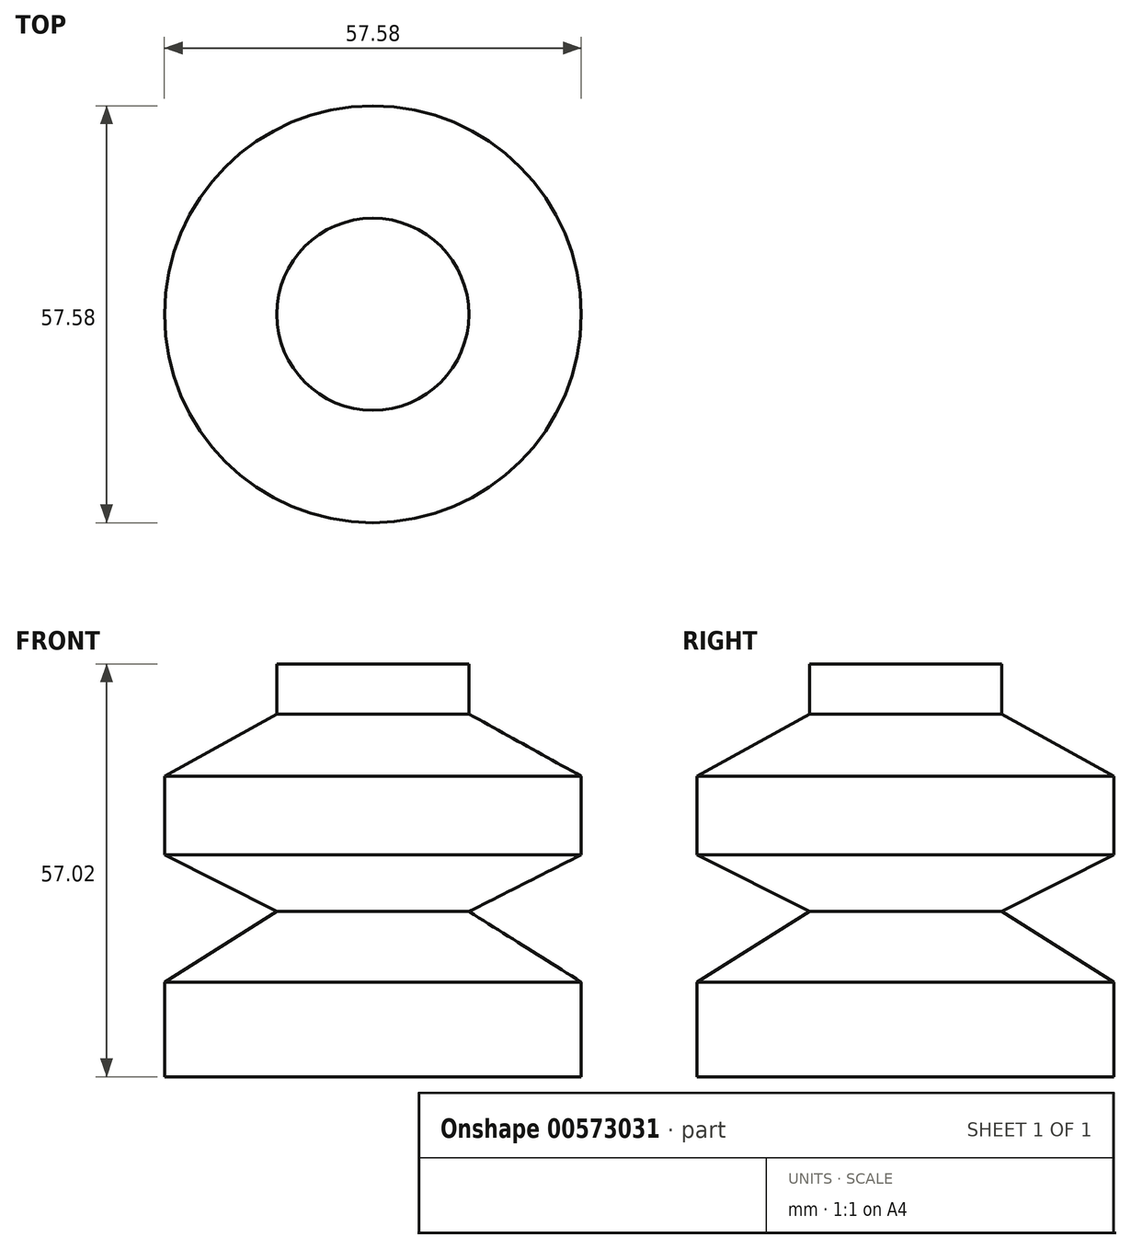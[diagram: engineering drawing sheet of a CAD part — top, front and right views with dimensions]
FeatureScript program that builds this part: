
annotation { "Feature Type Name" : "Feature", "Feature Type Description" : "" }
export const myFeature = defineFeature(function(context is Context, id is Id, definition is map)
    precondition{}
    {
        {
            var Q0;
            Q0=qCreatedBy(makeId("Front.planeOp"),FACE);
            var sketch = newSketch(context, id + "F0", { "sketchPlane" : qUnion([Q0])});
            skLineSegment(sketch, "E0", {"start": v(0, 0) * mm, "end": v(-28.79, 0) * mm});
            skLineSegment(sketch, "E1", {"start": v(-28.79, 0) * mm, "end": v(-28.79, 13.09) * mm});
            skLineSegment(sketch, "E2", {"start": v(-28.79, 13.09) * mm, "end": v(-13.27, 22.8) * mm});
            skLineSegment(sketch, "E3", {"start": v(-13.27, 22.8) * mm, "end": v(-28.79, 30.66) * mm});
            skLineSegment(sketch, "E4", {"start": v(-28.79, 30.66) * mm, "end": v(-28.79, 41.5) * mm});
            skLineSegment(sketch, "E5", {"start": v(-28.79, 41.5) * mm, "end": v(-13.27, 50.1) * mm});
            skLineSegment(sketch, "E6", {"start": v(-13.27, 50.1) * mm, "end": v(-13.27, 57.02) * mm});
            skLineSegment(sketch, "E7", {"start": v(-13.27, 57.02) * mm, "end": v(0, 57.02) * mm});
            skLineSegment(sketch, "E8", {"start": v(0, 57.02) * mm, "end": v(0, 0) * mm});
            skSolve(sketch);
        }
        {
            var Q0;
            Q0=makeQuery(id+"F0.imprint","IMPRINT",FACE,{"disambiguationData":[TD([[makeQuery(id+"F0.imprint","IMPRINT",EDGE,{"derivedFrom":sQuery(id+"F0.wireOp",EDGE,"E0")}),-1.0]])]});
            var Q1;
            Q1=sQuery(id+"F0.wireOp",EDGE,"E8");
            revolve(context, id + "F1", {"entities" : qUnion([Q0]), "axis" : qUnion([Q1]), "revolveType" : RevolveType.FULL});
        }
    });
